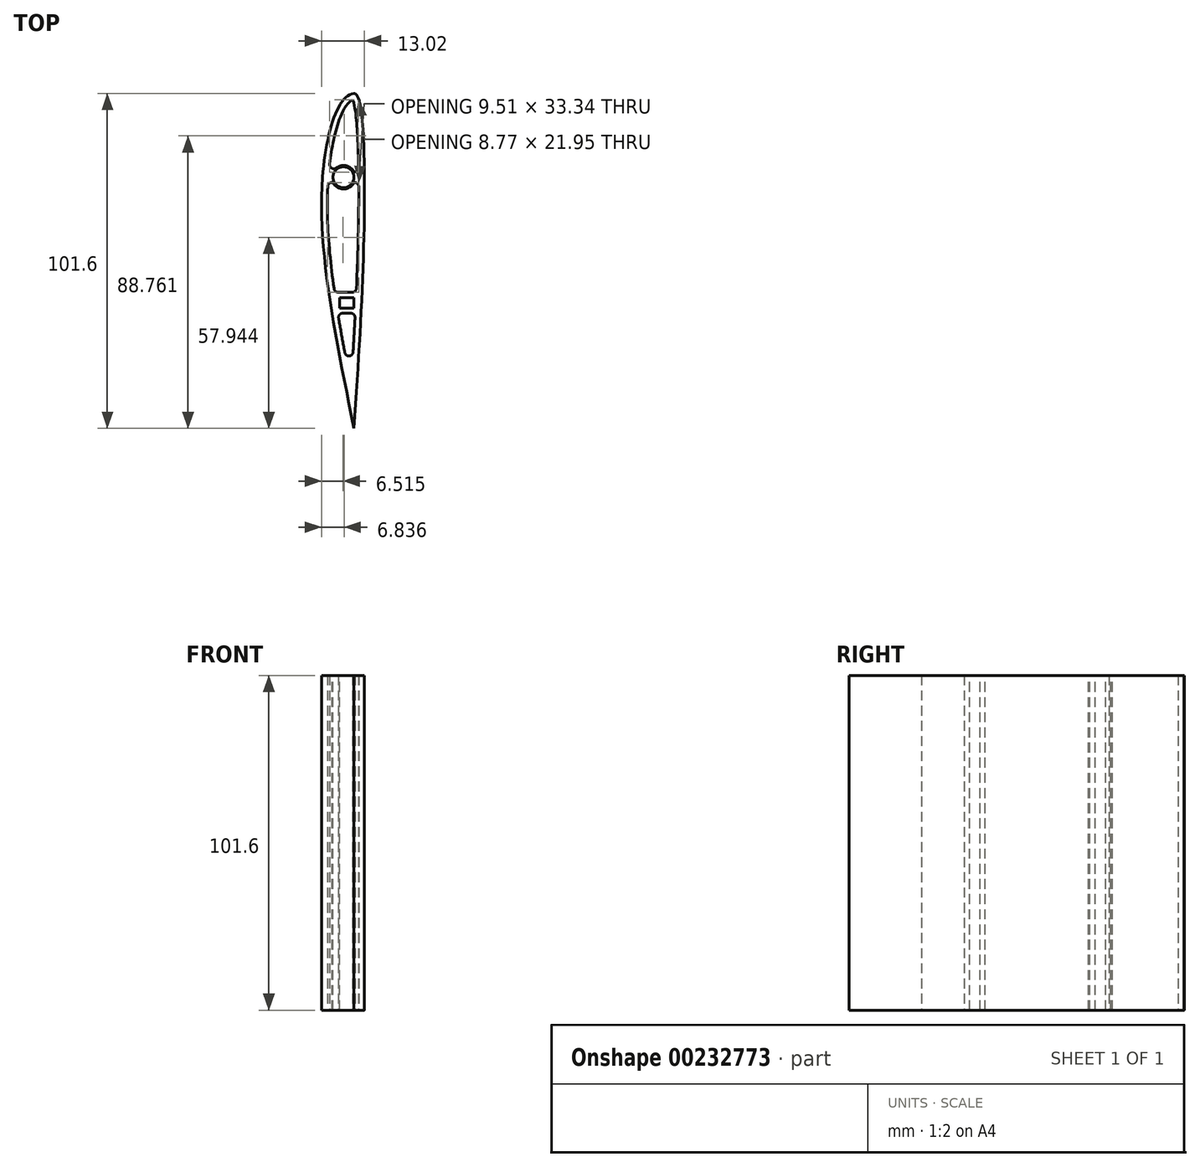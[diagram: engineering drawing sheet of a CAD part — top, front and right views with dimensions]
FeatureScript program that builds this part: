
annotation { "Feature Type Name" : "Feature", "Feature Type Description" : "" }
export const myFeature = defineFeature(function(context is Context, id is Id, definition is map)
    precondition{}
    {
        {
            var Q0;
            Q0=qCreatedBy(makeId("Top.planeOp"),FACE);
            var sketch = newSketch(context, id + "F0", { "sketchPlane" : qUnion([Q0])});
            skLineSegment(sketch, "E0", {"start": v(0, 25.4) * mm, "end": v(0, -76.2) * mm});
            skPoint(sketch, "E1", {"position": v(0, 0) * mm});
            skLineSegment(sketch, "E2", {"start": v(-9.53, 0) * mm, "end": v(3.18, 0) * mm});
            skFitSpline(sketch, "E3", {"points": [v(0, 25.4) * mm, v(-9.53, 0) * mm, v(0, -76.2) * mm], "startDerivative": vector(-40.87, -2.73) * mm, "endDerivative": vector(27.96, -138.22) * mm});
            skFitSpline(sketch, "E4", {"points": [v(0, 25.4) * mm, v(3.18, 0) * mm, v(0, -76.2) * mm], "startDerivative": vector(19.95, 2.1) * mm, "endDerivative": vector(-9.34, -136.52) * mm});
            skSolve(sketch);
        }
        {
            var Q0;
            Q0 = qSketchRegion(id + "F0", true);
            extrude(context, id + "F1", {"entities" : qUnion([Q0]), "depth" : 101.6 * mm});
        }
        {
            var Q0;
            Q0=makeQuery(id+"F1.opExtrude","CAP_FACE",FACE,{"disambiguationData":[OSD([sQuery(id+"F0.wireOp",EDGE,"E3"),sQuery(id+"F0.wireOp",EDGE,"E4")])],"isStart":false});
            var Q1;
            Q1=makeQuery(id+"F1.opExtrude","CAP_FACE",FACE,{"disambiguationData":[OSD([sQuery(id+"F0.wireOp",EDGE,"E3"),sQuery(id+"F0.wireOp",EDGE,"E4")])],"isStart":true});
            shell(context, id + "F2", {"entities" : qUnion([Q0, Q1]), "thickness" : 1.75 * mm});
        }
        {
            var Q0;
            Q0=makeQuery(id+"F1.opExtrude","CAP_FACE",FACE,{"disambiguationData":[OSD([sQuery(id+"F0.wireOp",EDGE,"E3"),sQuery(id+"F0.wireOp",EDGE,"E4")])],"isStart":false});
            var sketch = newSketch(context, id + "F3", { "sketchPlane" : qUnion([Q0])});
            skLineSegment(sketch, "E5", {"start": v(-7.77, 0) * mm, "end": v(1.43, 0) * mm, "construction": true});
            skCircle(sketch, "E6", {"center": v(-3.17, 0) * mm, "radius": 3.18 * mm});
            skCircle(sketch, "E7.0", {"center": v(-3.17, 0) * mm, "radius": 3.58 * mm});
            skPoint(sketch, "E8.start.orphan", {"position": v(-8.44, 1.59) * mm});
            skPoint(sketch, "E9.MirrorCS.start.orphan", {"position": v(-8.44, -1.59) * mm});
            skPoint(sketch, "E10.end.orphan", {"position": v(2.36, -1.59) * mm});
            skPoint(sketch, "E11.end.orphan", {"position": v(2.36, 1.59) * mm});
            skLineSegment(sketch, "E12.bottom", {"start": v(-8.64, 1.59) * mm, "end": v(-6.38, 1.59) * mm});
            skLineSegment(sketch, "E12.top", {"start": v(-8.64, -1.59) * mm, "end": v(-6.38, -1.59) * mm});
            skLineSegment(sketch, "E12.left", {"start": v(-8.64, 1.59) * mm, "end": v(-8.64, -1.59) * mm});
            skLineSegment(sketch, "E12.right", {"start": v(2.3, 1.59) * mm, "end": v(2.3, -1.59) * mm});
            skLineSegment(sketch, "E13.trimOffspring", {"start": v(0.03, 1.59) * mm, "end": v(2.3, 1.59) * mm});
            skLineSegment(sketch, "E14.trimOffspring", {"start": v(0.03, -1.59) * mm, "end": v(2.3, -1.59) * mm});
            skSolve(sketch);
        }
        {
            var Q0;
            Q0 = qSketchRegion(id + "F3", true);
            extrude(context, id + "F4", {"entities" : qUnion([Q0]), "operationType" : NewBodyOperationType.ADD, "oppositeDirection" : true, "depth" : 101.6 * mm});
        }
        {
            var Q0;
            Q0=makeQuery(id+"F4.boolean.opBoolean","MERGE",FACE,{"derivedFrom":[makeQuery(id+"F1.opExtrude","CAP_FACE",FACE,{"disambiguationData":[OSD([sQuery(id+"F0.wireOp",EDGE,"E3"),sQuery(id+"F0.wireOp",EDGE,"E4")])],"isStart":false}),makeQuery(id+"F4.opExtrude","CAP_FACE",FACE,{"disambiguationData":[OSD([sQuery(id+"F3.wireOp",EDGE,"E6"),sQuery(id+"F3.wireOp",EDGE,"E7.0"),sQuery(id+"F3.wireOp",EDGE,"E12.bottom"),sQuery(id+"F3.wireOp",EDGE,"E12.top"),sQuery(id+"F3.wireOp",EDGE,"E12.left"),sQuery(id+"F3.wireOp",EDGE,"E12.right"),sQuery(id+"F3.wireOp",EDGE,"E13.trimOffspring"),sQuery(id+"F3.wireOp",EDGE,"E14.trimOffspring")])],"isStart":true})]});
            var sketch = newSketch(context, id + "F5", { "sketchPlane" : qUnion([Q0])});
            skLineSegment(sketch, "E15", {"start": v(0, 0) * mm, "end": v(0, -34.92) * mm});
            skLineSegment(sketch, "E16.bottom", {"start": v(0, -36.51) * mm, "end": v(-4.36, -36.51) * mm});
            skLineSegment(sketch, "E16.top", {"start": v(0, -39.69) * mm, "end": v(-4.36, -39.69) * mm});
            skLineSegment(sketch, "E16.left", {"start": v(0, -36.51) * mm, "end": v(0, -39.69) * mm});
            skLineSegment(sketch, "E16.right", {"start": v(-4.36, -36.51) * mm, "end": v(-4.36, -39.69) * mm});
            skPoint(sketch, "E16.middle", {"position": v(-2.18, -38.1) * mm});
            skLineSegment(sketch, "E17.bottom", {"start": v(-6.14, -34.92) * mm, "end": v(1.78, -34.92) * mm});
            skLineSegment(sketch, "E17.top", {"start": v(-6.14, -41.27) * mm, "end": v(1.78, -41.27) * mm});
            skLineSegment(sketch, "E17.left", {"start": v(-6.14, -34.92) * mm, "end": v(-6.14, -41.27) * mm});
            skLineSegment(sketch, "E17.right", {"start": v(1.78, -34.92) * mm, "end": v(1.78, -41.27) * mm});
            skLineSegment(sketch, "E18.trimOffspring", {"start": v(0, -36.51) * mm, "end": v(0, -38.1) * mm});
            skPoint(sketch, "E19.orphan", {"position": v(1.54, -38.1) * mm});
            skPoint(sketch, "E20.orphan", {"position": v(-5.9, -38.1) * mm});
            skSolve(sketch);
        }
        {
            var Q0;
            Q0 = qSketchRegion(id + "F5", true);
            extrude(context, id + "F6", {"entities" : qUnion([Q0]), "operationType" : NewBodyOperationType.ADD, "oppositeDirection" : true, "depth" : 101.6 * mm});
        }
        {
            var Q0;
            Q0=makeQuery(id+"F4.boolean.opBoolean","INTERSECT",EDGE,{"derivedFrom":[makeQuery(id+"F2.opShell","OFFSET_FACE",FACE,{"disambiguationData":[OSD([sQuery(id+"F0.wireOp",EDGE,"E3")])]}),makeQuery(id+"F4.opExtrude","SWEPT_FACE",FACE,{"disambiguationData":[OSD([sQuery(id+"F3.wireOp",EDGE,"E12.bottom")])]})]});
            var Q1;
            Q1=makeQuery(id+"F4.boolean.opBoolean","INTERSECT",EDGE,{"derivedFrom":[makeQuery(id+"F2.opShell","OFFSET_FACE",FACE,{"disambiguationData":[OSD([sQuery(id+"F0.wireOp",EDGE,"E4")])]}),makeQuery(id+"F4.opExtrude","SWEPT_FACE",FACE,{"disambiguationData":[OSD([sQuery(id+"F3.wireOp",EDGE,"E13.trimOffspring")])]})]});
            var Q2;
            Q2=makeQuery(id+"F4.boolean.opBoolean","INTERSECT",EDGE,{"derivedFrom":[makeQuery(id+"F2.opShell","OFFSET_FACE",FACE,{"disambiguationData":[OSD([sQuery(id+"F0.wireOp",EDGE,"E4")])]}),makeQuery(id+"F4.opExtrude","SWEPT_FACE",FACE,{"disambiguationData":[OSD([sQuery(id+"F3.wireOp",EDGE,"E14.trimOffspring")])]})]});
            var Q3;
            Q3=makeQuery(id+"F4.boolean.opBoolean","INTERSECT",EDGE,{"derivedFrom":[makeQuery(id+"F2.opShell","OFFSET_FACE",FACE,{"disambiguationData":[OSD([sQuery(id+"F0.wireOp",EDGE,"E3")])]}),makeQuery(id+"F4.opExtrude","SWEPT_FACE",FACE,{"disambiguationData":[OSD([sQuery(id+"F3.wireOp",EDGE,"E12.top")])]})]});
            fillet(context, id + "F7", {"entities" : qUnion([Q0, Q1, Q2, Q3]), "radius" : 1.27 * mm, "tangentPropagation" : true, "allowEdgeOverflow" : false});
        }
        {
            var Q0;
            Q0=makeQuery(id+"F4.opExtrude","SWEPT_EDGE",EDGE,{"disambiguationData":[OSD([sQuery(id+"F3.wireOp",EDGE,"E7.0"),sQuery(id+"F3.wireOp",EDGE,"E12.top")])]});
            var Q1;
            Q1=makeQuery(id+"F4.opExtrude","SWEPT_EDGE",EDGE,{"disambiguationData":[OSD([sQuery(id+"F3.wireOp",EDGE,"E7.0"),sQuery(id+"F3.wireOp",EDGE,"E14.trimOffspring")])]});
            var Q2;
            Q2=makeQuery(id+"F4.opExtrude","SWEPT_EDGE",EDGE,{"disambiguationData":[OSD([sQuery(id+"F3.wireOp",EDGE,"E7.0"),sQuery(id+"F3.wireOp",EDGE,"E13.trimOffspring")])]});
            var Q3;
            {var subQ0=sQuery(id+"F3.wireOp",EDGE,"E12.bottom");var subQ1=sQuery(id+"F3.wireOp",EDGE,"E7.0");Q3=makeQuery(id+"F7.opFillet","BLEND_EDGE",EDGE,{"blendedFrom":[makeQuery(id+"F4.boolean.opBoolean","INTERSECT",EDGE,{"derivedFrom":[makeQuery(id+"F2.opShell","OFFSET_FACE",FACE,{"disambiguationData":[OSD([sQuery(id+"F0.wireOp",EDGE,"E3")])]}),makeQuery(id+"F4.opExtrude","SWEPT_FACE",FACE,{"disambiguationData":[OSD([subQ0])]})]}),makeQuery(id+"F4.opExtrude","SWEPT_FACE",FACE,{"disambiguationData":[OSD([subQ1]),TDD([makeQuery(id+"F3.imprint","IMPRINT",EDGE,{"disambiguationData":[TD([[makeQuery(id+"F3.imprint","INTERSECT",VERTEX,{"derivedFrom":[subQ1,subQ0]}),1.0]])],"derivedFrom":subQ1})])]})],"blendedInto":[makeQuery(id+"F4.opExtrude","SWEPT_FACE",FACE,{"disambiguationData":[OSD([subQ1]),TDD([makeQuery(id+"F3.imprint","IMPRINT",EDGE,{"disambiguationData":[TD([[makeQuery(id+"F3.imprint","INTERSECT",VERTEX,{"derivedFrom":[subQ1,subQ0]}),1.0]])],"derivedFrom":subQ1})])]})]});}
            fillet(context, id + "F8", {"entities" : qUnion([Q0, Q1, Q2, Q3]), "radius" : 1.27 * mm, "tangentPropagation" : true, "allowEdgeOverflow" : false});
        }
        {
            var Q0;
            {var subQ4=sQuery(id+"F3.wireOp",EDGE,"E12.top");var subQ9=sQuery(id+"F0.wireOp",EDGE,"E3");Q0=makeQuery(id+"F6.boolean.opBoolean","INTERSECT",EDGE,{"derivedFrom":[makeQuery(id+"F4.boolean.opBoolean","SPLIT",FACE,{"disambiguationData":[TD([makeQuery(id+"F4.opExtrude","SWEPT_FACE",FACE,{"disambiguationData":[OSD([subQ4])]})])],"derivedFrom":makeQuery(id+"F2.opShell","OFFSET_FACE",FACE,{"disambiguationData":[OSD([subQ9])]})}),makeQuery(id+"F6.opExtrude","SWEPT_FACE",FACE,{"disambiguationData":[OSD([sQuery(id+"F5.wireOp",EDGE,"E17.bottom")])]})]});}
            var Q1;
            {var subQ0=sQuery(id+"F3.wireOp",EDGE,"E14.trimOffspring");var subQ8=sQuery(id+"F0.wireOp",EDGE,"E4");Q1=makeQuery(id+"F6.boolean.opBoolean","INTERSECT",EDGE,{"derivedFrom":[makeQuery(id+"F4.boolean.opBoolean","SPLIT",FACE,{"disambiguationData":[TD([makeQuery(id+"F4.opExtrude","SWEPT_FACE",FACE,{"disambiguationData":[OSD([subQ0])]})])],"derivedFrom":makeQuery(id+"F2.opShell","OFFSET_FACE",FACE,{"disambiguationData":[OSD([subQ8])]})}),makeQuery(id+"F6.opExtrude","SWEPT_FACE",FACE,{"disambiguationData":[OSD([sQuery(id+"F5.wireOp",EDGE,"E17.bottom")])]})]});}
            var Q2;
            {var subQ4=sQuery(id+"F3.wireOp",EDGE,"E12.top");var subQ9=sQuery(id+"F0.wireOp",EDGE,"E3");Q2=makeQuery(id+"F6.boolean.opBoolean","INTERSECT",EDGE,{"derivedFrom":[makeQuery(id+"F4.boolean.opBoolean","SPLIT",FACE,{"disambiguationData":[TD([makeQuery(id+"F4.opExtrude","SWEPT_FACE",FACE,{"disambiguationData":[OSD([subQ4])]})])],"derivedFrom":makeQuery(id+"F2.opShell","OFFSET_FACE",FACE,{"disambiguationData":[OSD([subQ9])]})}),makeQuery(id+"F6.opExtrude","SWEPT_FACE",FACE,{"disambiguationData":[OSD([sQuery(id+"F5.wireOp",EDGE,"E17.top")])]})]});}
            var Q3;
            {var subQ0=sQuery(id+"F3.wireOp",EDGE,"E14.trimOffspring");var subQ8=sQuery(id+"F0.wireOp",EDGE,"E4");Q3=makeQuery(id+"F6.boolean.opBoolean","INTERSECT",EDGE,{"derivedFrom":[makeQuery(id+"F4.boolean.opBoolean","SPLIT",FACE,{"disambiguationData":[TD([makeQuery(id+"F4.opExtrude","SWEPT_FACE",FACE,{"disambiguationData":[OSD([subQ0])]})])],"derivedFrom":makeQuery(id+"F2.opShell","OFFSET_FACE",FACE,{"disambiguationData":[OSD([subQ8])]})}),makeQuery(id+"F6.opExtrude","SWEPT_FACE",FACE,{"disambiguationData":[OSD([sQuery(id+"F5.wireOp",EDGE,"E17.top")])]})]});}
            fillet(context, id + "F9", {"entities" : qUnion([Q0, Q1, Q2, Q3]), "radius" : 1.27 * mm, "tangentPropagation" : true, "allowEdgeOverflow" : false});
        }
        {
            var Q0;
            {var subQ0=sQuery(id+"F0.wireOp",EDGE,"E4");var subQ1=sQuery(id+"F0.wireOp",EDGE,"E3");var subQ2=sQuery(id+"F0.wireOp",EDGE,"E0");Q0=makeQuery(id+"F2.opShell","OFFSET_EDGE",EDGE,{"disambiguationData":[OSD([subQ2,subQ1,subQ0]),TDD([makeQuery(id+"F1.opExtrude","SWEPT_EDGE",EDGE,{"disambiguationData":[OSD([subQ2,subQ1,subQ0]),TDD([makeQuery(id+"F0.imprint","INTERSECT",VERTEX,{"disambiguationData":[OD(1.0)],"derivedFrom":[subQ2,subQ1,subQ0]})])]})])]});}
            fillet(context, id + "F10", {"entities" : qUnion([Q0]), "radius" : 1.27 * mm, "tangentPropagation" : true, "allowEdgeOverflow" : false});
        }
    });
